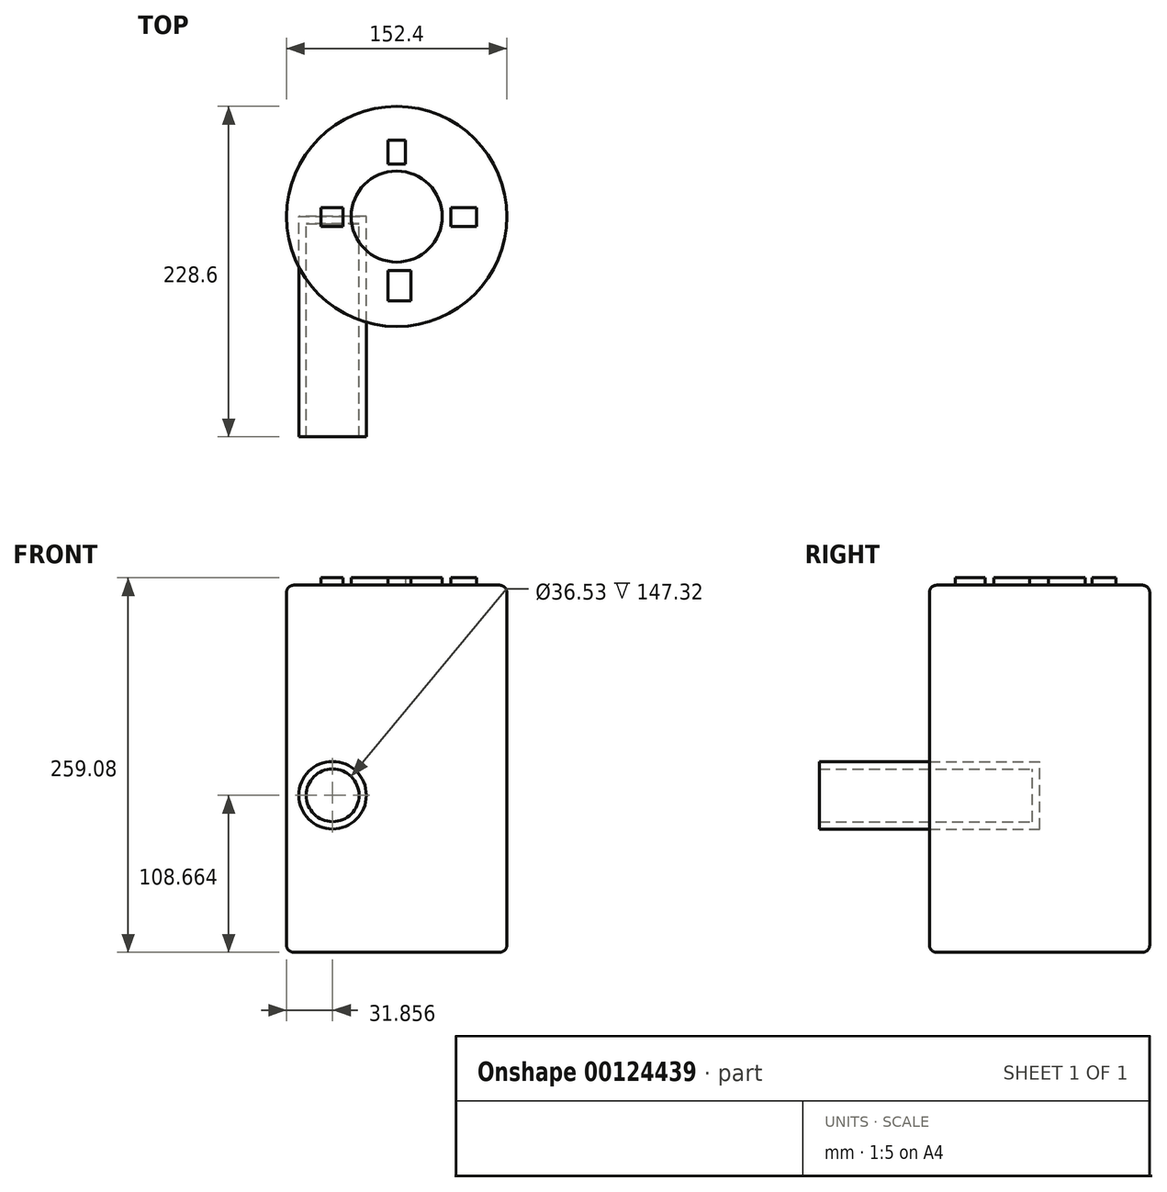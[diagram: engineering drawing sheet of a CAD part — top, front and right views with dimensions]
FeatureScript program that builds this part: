
annotation { "Feature Type Name" : "Feature", "Feature Type Description" : "" }
export const myFeature = defineFeature(function(context is Context, id is Id, definition is map)
    precondition{}
    {
        {
            var Q0;
            Q0=qCreatedBy(makeId("Top.planeOp"),FACE);
            var sketch = newSketch(context, id + "F0", { "sketchPlane" : qUnion([Q0])});
            skCircle(sketch, "E0", {"center": v(0, 0) * mm, "radius": 76.2 * mm});
            skSolve(sketch);
        }
        {
            var Q0;
            Q0=makeQuery(id+"F0.imprint","IMPRINT",FACE,{"disambiguationData":[TD([[makeQuery(id+"F0.imprint","IMPRINT",EDGE,{"derivedFrom":sQuery(id+"F0.wireOp",EDGE,"E0")}),1.0]])]});
            extrude(context, id + "F1", {"entities" : qUnion([Q0]), "depth" : 254 * mm});
        }
        {
            var Q0;
            Q0=makeQuery(id+"F1.opExtrude","CAP_FACE",FACE,{"disambiguationData":[OSD([sQuery(id+"F0.wireOp",EDGE,"E0")])],"isStart":false});
            var sketch = newSketch(context, id + "F2", { "sketchPlane" : qUnion([Q0])});
            skCircle(sketch, "E1", {"center": v(0, 0) * mm, "radius": 31.5 * mm});
            skSolve(sketch);
        }
        {
            var Q0;
            Q0=makeQuery(id+"F2.imprint","IMPRINT",FACE,{"disambiguationData":[TD([[makeQuery(id+"F2.imprint","IMPRINT",EDGE,{"derivedFrom":sQuery(id+"F2.wireOp",EDGE,"E1")}),1.0]])]});
            extrude(context, id + "F3", {"entities" : qUnion([Q0]), "depth" : 5.08 * mm});
        }
        {
            var Q0;
            Q0=makeQuery(id+"F3.opExtrude","CAP_FACE",FACE,{"disambiguationData":[OSD([sQuery(id+"F2.wireOp",EDGE,"E1")])],"isStart":false});
            shell(context, id + "F4", {"entities" : qUnion([Q0]), "thickness" : 5.08 * mm});
        }
        {
            var Q0;
            Q0=makeQuery(id+"F1.opExtrude","CAP_EDGE",EDGE,{"disambiguationData":[OSD([sQuery(id+"F0.wireOp",EDGE,"E0")])],"isStart":false});
            fillet(context, id + "F5", {"entities" : qUnion([Q0]), "radius" : 5.08 * mm, "tangentPropagation" : true, "allowEdgeOverflow" : false});
        }
        {
            var Q0;
            Q0=makeQuery(id+"F1.opExtrude","CAP_EDGE",EDGE,{"disambiguationData":[OSD([sQuery(id+"F0.wireOp",EDGE,"E0")])],"isStart":true});
            fillet(context, id + "F6", {"entities" : qUnion([Q0]), "radius" : 5.08 * mm, "tangentPropagation" : true, "allowEdgeOverflow" : false});
        }
        {
            var Q0;
            Q0=makeQuery(id+"F1.opExtrude","CAP_FACE",FACE,{"disambiguationData":[OSD([sQuery(id+"F0.wireOp",EDGE,"E0")])],"isStart":false});
            var sketch = newSketch(context, id + "F7", { "sketchPlane" : qUnion([Q0])});
            skLineSegment(sketch, "E2.bottom", {"start": v(-52.23, -6.8) * mm, "end": v(-37.2, -6.8) * mm});
            skLineSegment(sketch, "E2.top", {"start": v(-52.23, 6.08) * mm, "end": v(-37.2, 6.08) * mm});
            skLineSegment(sketch, "E2.left", {"start": v(-52.23, -6.8) * mm, "end": v(-52.23, 6.08) * mm});
            skLineSegment(sketch, "E2.right", {"start": v(-37.2, -6.8) * mm, "end": v(-37.2, 6.08) * mm});
            skSolve(sketch);
        }
        {
            var Q0;
            Q0=makeQuery(id+"F7.imprint","IMPRINT",FACE,{"disambiguationData":[TD([[makeQuery(id+"F7.imprint","IMPRINT",EDGE,{"derivedFrom":sQuery(id+"F7.wireOp",EDGE,"E2.bottom")}),1.0]])]});
            extrude(context, id + "F8", {"entities" : qUnion([Q0]), "depth" : 5.08 * mm});
        }
        {
            var Q0;
            Q0=makeQuery(id+"F1.opExtrude","CAP_FACE",FACE,{"disambiguationData":[OSD([sQuery(id+"F0.wireOp",EDGE,"E0")])],"isStart":false});
            var sketch = newSketch(context, id + "F9", { "sketchPlane" : qUnion([Q0])});
            skLineSegment(sketch, "E3.bottom", {"start": v(-6.02, 52.69) * mm, "end": v(6.02, 52.69) * mm});
            skLineSegment(sketch, "E3.top", {"start": v(-6.02, 36.43) * mm, "end": v(6.02, 36.43) * mm});
            skLineSegment(sketch, "E3.left", {"start": v(-6.02, 52.69) * mm, "end": v(-6.02, 36.43) * mm});
            skLineSegment(sketch, "E3.right", {"start": v(6.02, 52.69) * mm, "end": v(6.02, 36.43) * mm});
            skSolve(sketch);
        }
        {
            var Q0;
            Q0=makeQuery(id+"F9.imprint","IMPRINT",FACE,{"disambiguationData":[TD([[makeQuery(id+"F9.imprint","IMPRINT",EDGE,{"derivedFrom":sQuery(id+"F9.wireOp",EDGE,"E3.bottom")}),-1.0]])]});
            extrude(context, id + "F10", {"entities" : qUnion([Q0]), "depth" : 5.08 * mm});
        }
        {
            var Q0;
            Q0=makeQuery(id+"F1.opExtrude","CAP_FACE",FACE,{"disambiguationData":[OSD([sQuery(id+"F0.wireOp",EDGE,"E0")])],"isStart":false});
            var sketch = newSketch(context, id + "F11", { "sketchPlane" : qUnion([Q0])});
            skLineSegment(sketch, "E4.bottom", {"start": v(37.57, 6.08) * mm, "end": v(55.13, 6.08) * mm});
            skLineSegment(sketch, "E4.top", {"start": v(37.57, -6.83) * mm, "end": v(55.13, -6.83) * mm});
            skLineSegment(sketch, "E4.left", {"start": v(37.57, 6.08) * mm, "end": v(37.57, -6.83) * mm});
            skLineSegment(sketch, "E4.right", {"start": v(55.13, 6.08) * mm, "end": v(55.13, -6.83) * mm});
            skSolve(sketch);
        }
        {
            var Q0;
            Q0=makeQuery(id+"F11.imprint","IMPRINT",FACE,{"disambiguationData":[TD([[makeQuery(id+"F11.imprint","IMPRINT",EDGE,{"derivedFrom":sQuery(id+"F11.wireOp",EDGE,"E4.bottom")}),-1.0]])]});
            extrude(context, id + "F12", {"entities" : qUnion([Q0]), "depth" : 5.08 * mm});
        }
        {
            var Q0;
            Q0=makeQuery(id+"F1.opExtrude","CAP_FACE",FACE,{"disambiguationData":[OSD([sQuery(id+"F0.wireOp",EDGE,"E0")])],"isStart":false});
            var sketch = newSketch(context, id + "F13", { "sketchPlane" : qUnion([Q0])});
            skLineSegment(sketch, "E5.bottom", {"start": v(-6.02, -37.52) * mm, "end": v(9.8, -37.52) * mm});
            skLineSegment(sketch, "E5.top", {"start": v(-6.02, -58.38) * mm, "end": v(9.8, -58.38) * mm});
            skLineSegment(sketch, "E5.left", {"start": v(-6.02, -37.52) * mm, "end": v(-6.02, -58.38) * mm});
            skLineSegment(sketch, "E5.right", {"start": v(9.8, -37.52) * mm, "end": v(9.8, -58.38) * mm});
            skSolve(sketch);
        }
        {
            var Q0;
            Q0=makeQuery(id+"F13.imprint","IMPRINT",FACE,{"disambiguationData":[TD([[makeQuery(id+"F13.imprint","IMPRINT",EDGE,{"derivedFrom":sQuery(id+"F13.wireOp",EDGE,"E5.bottom")}),-1.0]])]});
            extrude(context, id + "F14", {"entities" : qUnion([Q0]), "depth" : 5.08 * mm});
        }
        {
            var Q0;
            Q0=qCreatedBy(makeId("Front.planeOp"),FACE);
            var sketch = newSketch(context, id + "F15", { "sketchPlane" : qUnion([Q0])});
            skCircle(sketch, "E6", {"center": v(-44.34, -31.48) * mm, "radius": 23.35 * mm});
            skSolve(sketch);
        }
        {
            var Q0;
            Q0=makeQuery(id+"F15.imprint","IMPRINT",FACE,{"disambiguationData":[TD([[makeQuery(id+"F15.imprint","IMPRINT",EDGE,{"derivedFrom":sQuery(id+"F15.wireOp",EDGE,"E6")}),1.0]])]});
            extrude(context, id + "F16", {"entities" : qUnion([Q0]), "depth" : 152.4 * mm});
        }
        {
            var Q0;
            Q0=makeQuery(id+"F16.opExtrude","SWEPT_BODY",BODY,{"disambiguationData":[OSD([sQuery(id+"F15.wireOp",EDGE,"E6")])]});
            var Q1;
            Q1=makeQuery(id+"F1.opExtrude","CAP_FACE",FACE,{"disambiguationData":[OSD([sQuery(id+"F0.wireOp",EDGE,"E0")])],"isStart":false});
            transform(context, id + "F17", {"entities" : qUnion([Q0]), "transformType" : TransformType.TRANSLATION_DISTANCE, "transformDirection" : qUnion([Q1]), "distance" : 140.14 * mm, "makeCopy" : false});
        }
        {
            var Q0;
            Q0=makeQuery(id+"F16.opExtrude","CAP_FACE",FACE,{"disambiguationData":[OSD([sQuery(id+"F15.wireOp",EDGE,"E6")])],"isStart":false});
            shell(context, id + "F18", {"entities" : qUnion([Q0]), "thickness" : 5.08 * mm});
        }
    });
